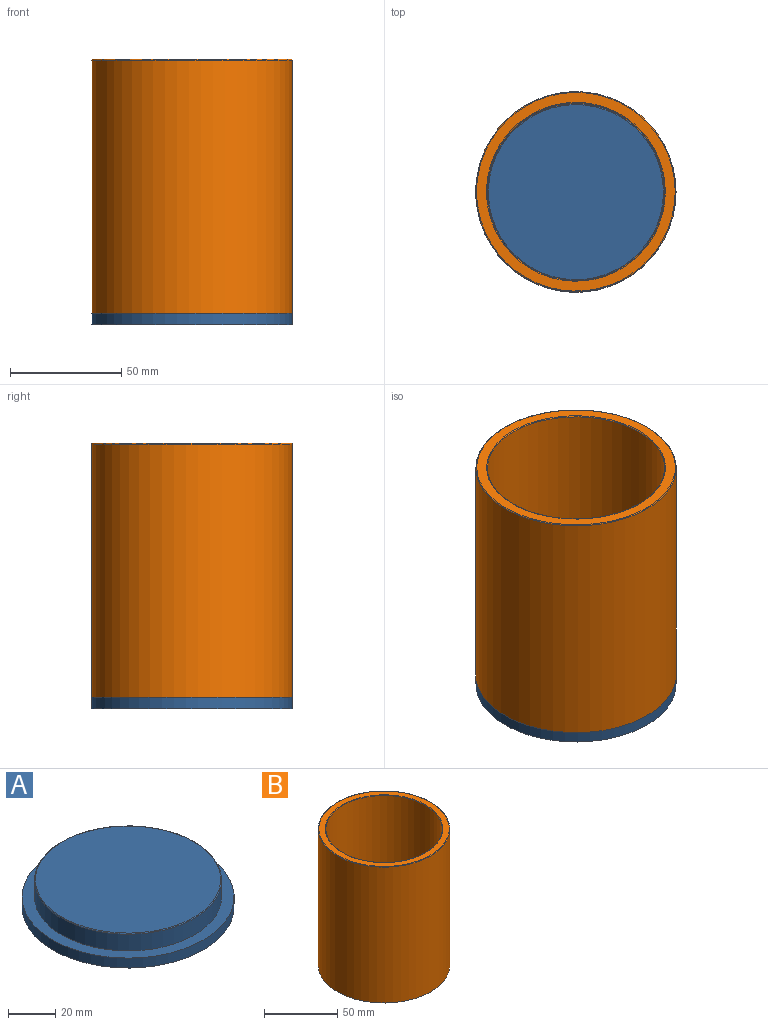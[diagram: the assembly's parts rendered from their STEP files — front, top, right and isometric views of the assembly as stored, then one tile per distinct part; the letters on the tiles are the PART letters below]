
ASSEMBLY  parts=2 mates=1
PART A: 6 faces, bbox 90x90x14.2 mm
  f0: plane 78.68x78.68mm, normal (0,0,1), area 4862.2mm2, adj f1
  f1: torus R=39.34mm, axis (0,0,1), area 136.7mm2, adj f0,f2
  f2: cylinder r=39.69mm len=79.38mm, axis (0,0,1), area 2157.2mm2, adj f1,f3
  f3: plane 90x90mm, normal (0,0,1), area 1412.6mm2, adj f2,f4
  f4: cylinder r=45mm len=90mm, axis (0,0,1), area 1458.8mm2, adj f3,f5
  f5: plane 90x90mm, normal (0,0,-1), area 6361.7mm2, adj f4
PART B: 6 faces, bbox 97.4x97.4x114.2 mm
  f0: cylinder r=45mm len=113.81mm, axis (0,0,1), area 32178.8mm2, adj f1,f5
  f1: plane 90x90mm, normal (0,0,-1), area 1375.1mm2, adj f0,f2
  f2: cylinder r=39.84mm len=113.81mm, axis (0,0,1), area 28489.5mm2, adj f1,f3
  f3: torus R=40.19mm, axis (0,0,1), area 138.1mm2, adj f2,f4
  f4: plane 89.3x89.3mm, normal (0,0,1), area 1188.6mm2, adj f3,f5
  f5: torus R=44.65mm, axis (0,0,1), area 155mm2, adj f0,f4
PLACE A t=(-104.09,-50.62,7.13)mm
PLACE B t=(-104.09,-50.62,39.37)mm
MATE fastened B.f0 <-> A.f1  axis (0,0,1) through (-104.09,-50.62,12.29)mm
